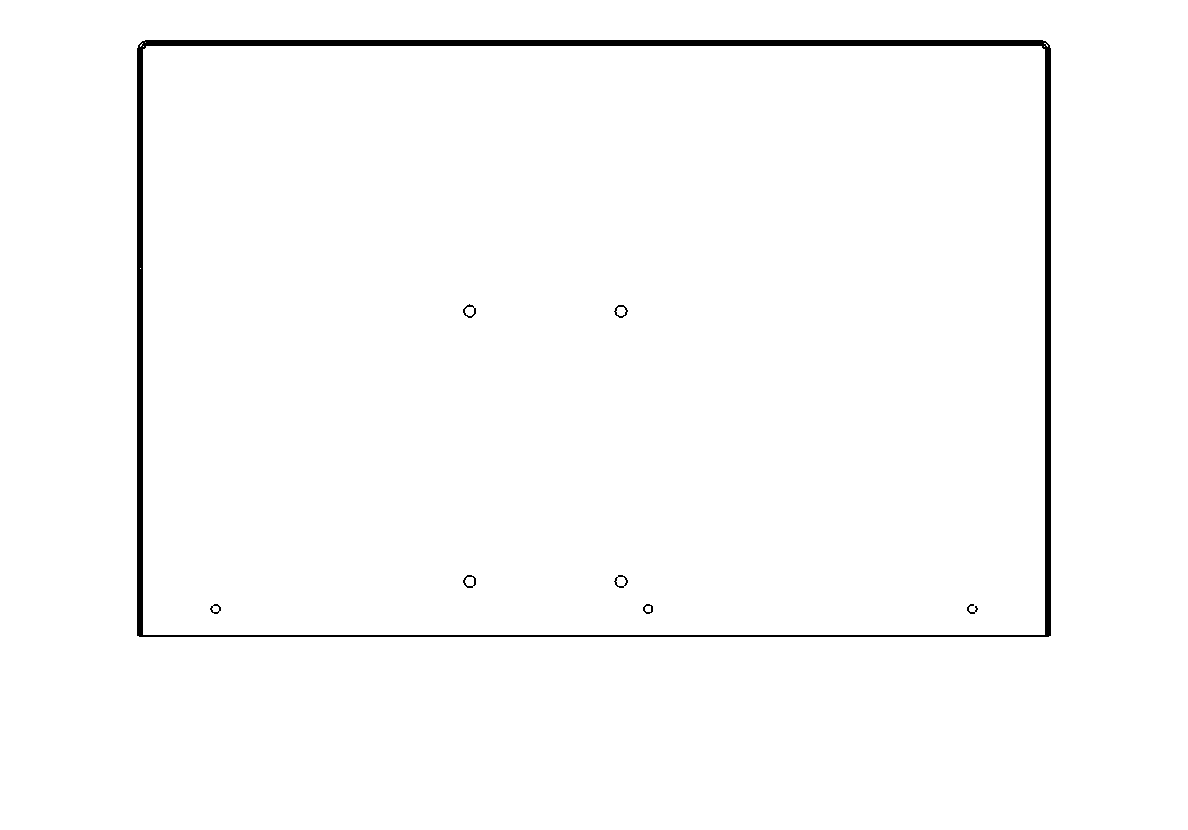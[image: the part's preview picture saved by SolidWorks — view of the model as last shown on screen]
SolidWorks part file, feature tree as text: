
SOLIDWORKS PART (.sldprt)
format: sldprt  version: not decoded by parser v0  size: 899,584 bytes
history: native  units: mm
features: sketch x13, cut_extrude x8, sheet_metal_op x6, pattern_linear x5, material x1 + 3 further entries (+12 scaffold rows collapsed)
feature tree (48):
  "Annotations"  RD1=279.400166mm
  scaffold x12  (default folders/planes/origin — collapsed)
  material  "Material <not specified>"
  "Design Table"
  sketch  "Sketch1"  dims[Chassi Height=128.3424mm Width=424.18mm D1=425.45mm]
  sheet_metal_op  "Sheet-Metal1"  Bend Radius=1.778mm Thickness=1.2192mm
  sheet_metal_op  "Base-Flange"
  sheet_metal_op  "BaseBend2"  Length=279.4mm
  sketch  "Sketch16"  dims[D1=15.24mm]
  sheet_metal_op  "Miterbend8"
  sheet_metal_op  "Miterbend9"
  sheet_metal_op  "Miterbend10"
  sketch  "Sketch17"  dims[D1=4.1402mm D2=34.925mm D3=12.7mm D4=139.7mm D5=12.7mm D6=215.9mm]
  cut_extrude  "Cut-Extrude1"  [1 undecoded]
  sketch  "Sketch20"  dims[c1.D4=6.35mm c1.D7=5.4102mm c2.D4=5.4102mm c2.D6=5.4102mm c3.D4=4.7752mm c3.D1=90.0deg c3.D2=412.75mm c3.D3=6.35mm c4.D4=106.68mm c4.D5=10.16mm c4.D6=3.81mm c5.D5=7.2898mm c5.D3=44.45mm c5.D4=88.9mm c5.D6=5.715mm c5.D1=6.35mm c5.D2=6.35mm c6.D5=9.1948mm c6.Panel Mounts Vertical Location=44.45mm c7.D5=~391.335457mm c7.D4=79.502mm c7.D3=63.2634mm c8.D4=88.9mm c8.D5=6.35mm c8.D6=8.509mm]
  cut_extrude  "Cut-Extrude3"  [1 undecoded]
  sketch  "Sketch21"  dims[c1.8-32 Pem Nut=5.4102mm c1.D4=5.4102mm c1.D5=5.4102mm c1.D2=12.7mm c1.D3=11.938mm c2.D4=11.938mm c2.Center Mounting Hole=127.0mm]
  cut_extrude  "Cut-Extrude4"  [1 undecoded]
  sketch  "Sketch22"  dims[D1=9.525mm D2=6.35mm D3=105.6894mm D4=68.58mm]
  cut_extrude  "Cut-Extrude5"  Depth=2.54mm
  pattern_linear  "LPattern1"  Count1=4 Count2=1 Spacing1=111.76mm Spacing2=50mm
  sketch  "Sketch23"  dims[D1=5.4102mm D2=34.036mm D3=96.3422mm]
  sketch  "Sketch24"  dims[c1.D9=5.4102mm c1.D10=5.4102mm c1.D11=5.4102mm c1.D12=5.4102mm c1.D2=5.4102mm c1.D3=5.4102mm c1.D4=5.4102mm c2.D2=5.4102mm c2.D3=5.4102mm c2.D4=5.4102mm c2.D1=124.079mm c3.D2=160.909mm c3.D3=15.748mm c3.D4=76.2mm c3.D5=81.28mm c3.D6=21.336mm c3.D7=117.348mm c3.D8=63.5mm]
  cut_extrude  "NIC Mount holes"  Depth=2.54mm
  sketch  "Sketch25"  dims[c1.D1=5.4102mm c1.D5=5.4102mm c1.D6=5.4102mm c2.D1=~103.342471mm c2.D2=91.44mm c2.D3=16.51mm c2.D4=17.78mm c2.D7=64.516mm c2.D8=10.668mm]
  cut_extrude  "Front COnn Holes"  Depth=2.54mm
  sketch  "lcd bottom cutout"  dims[D1=2.54mm D2=2.54mm D3=1.27mm]
  cut_extrude  "Cut-Extrude11"  Depth=2.54mm
  sketch  "Sketch26"  dims[D1=5.4102mm]
  sketch  "Sketch27"  dims[D1=4.191mm D2=4.191mm]
  cut_extrude  "Cut-Extrude12"  Depth=2.54mm
  "Flat-Pattern1"
  sketch  "Bend-Lines1"
  pattern_linear  "Flatten-<BaseBend2>1"  [2 undecoded]
  pattern_linear  "Flatten-<Miterbend8>1"  [2 undecoded]
  pattern_linear  "Flatten-<Miterbend9>1"  [2 undecoded]
  pattern_linear  "Flatten-<Miterbend10>1"  Spacing1=19.05mm Spacing2=6.35mm Front Flange=19.05mm Slot Position-x=6.35mm Slot Spacing-Y=57.15mm Slot From Top=37.592mm  [1 undecoded]
decode coverage: 21 of 32 modeling features carry decoded parameters; 3 rows unclassified (native names shown)
note: ~ marks probable driven/reference dimensions
note: 10 parameter values undecoded
summary: no parameter record found for 3 features
note: suppression state not decoded; provenance and decode notes live in map.json
